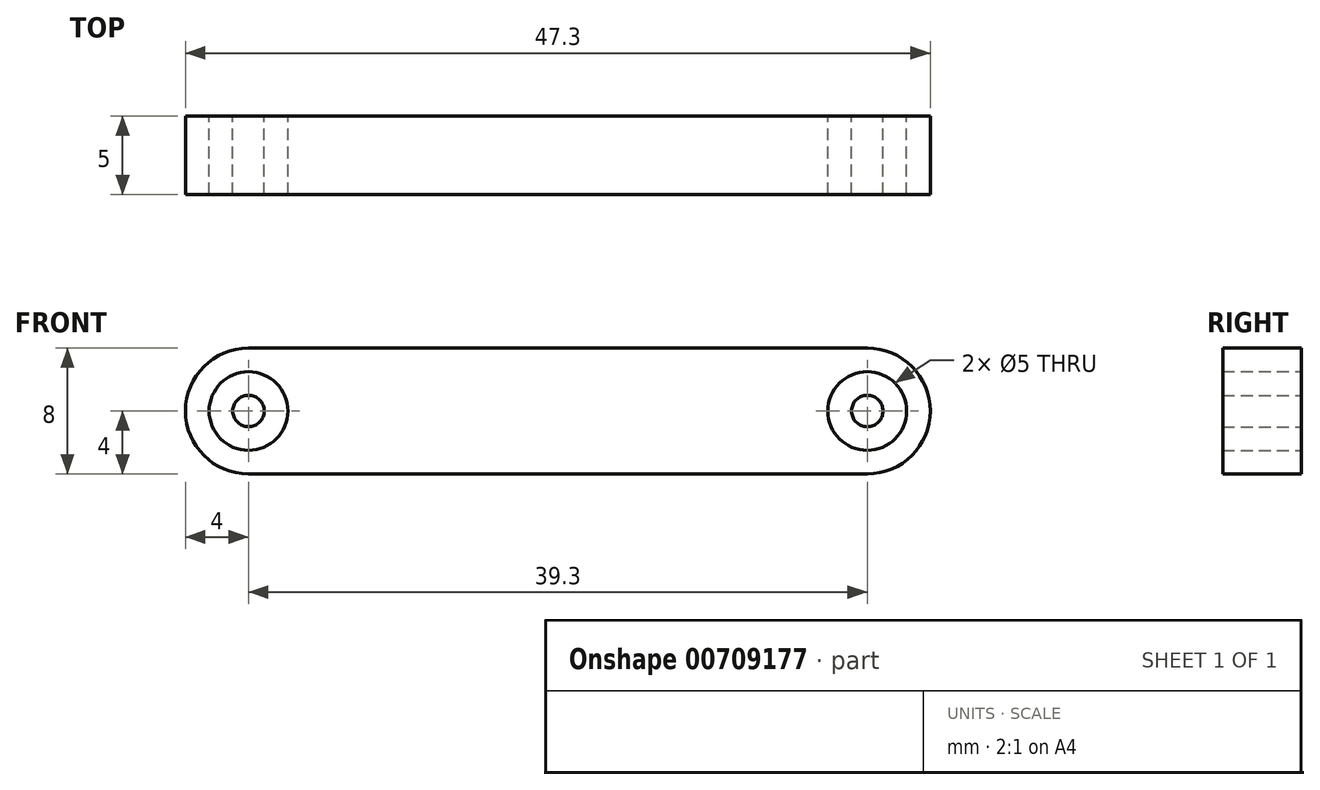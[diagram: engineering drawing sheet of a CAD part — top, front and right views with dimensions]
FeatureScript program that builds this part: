
annotation { "Feature Type Name" : "Feature", "Feature Type Description" : "" }
export const myFeature = defineFeature(function(context is Context, id is Id, definition is map)
    precondition{}
    {
        {
            var Q0;
            Q0=qCreatedBy(makeId("Front.planeOp"),FACE);
            var sketch = newSketch(context, id + "F0", { "sketchPlane" : qUnion([Q0])});
            skArc(sketch, "E0", {"start": v(0, 4) * mm, "mid": v(-4, 0) * mm, "end": v(0, -4) * mm});
            skArc(sketch, "E1", {"start": v(39.3, -4) * mm, "mid": v(43.3, 0) * mm, "end": v(39.3, 4) * mm});
            skLineSegment(sketch, "E2", {"start": v(0, 4) * mm, "end": v(39.3, 4) * mm});
            skLineSegment(sketch, "E3", {"start": v(0, -4) * mm, "end": v(39.3, -4) * mm});
            skCircle(sketch, "E4", {"center": v(0, 0) * mm, "radius": 2.5 * mm});
            skCircle(sketch, "E5", {"center": v(0, 0) * mm, "radius": 1 * mm});
            skCircle(sketch, "E6", {"center": v(39.3, 0) * mm, "radius": 2.5 * mm});
            skCircle(sketch, "E7", {"center": v(39.3, 0) * mm, "radius": 1 * mm});
            skSolve(sketch);
        }
        {
            var Q0;
            Q0=makeQuery(id+"F0.imprint","IMPRINT",FACE,{"disambiguationData":[TD([[makeQuery(id+"F0.imprint","IMPRINT",EDGE,{"derivedFrom":sQuery(id+"F0.wireOp",EDGE,"E0")}),1.0]])]});
            var Q1;
            Q1=makeQuery(id+"F0.imprint","IMPRINT",FACE,{"disambiguationData":[TD([[makeQuery(id+"F0.imprint","IMPRINT",EDGE,{"derivedFrom":sQuery(id+"F0.wireOp",EDGE,"E5")}),1.0]])]});
            var Q2;
            Q2=makeQuery(id+"F0.imprint","IMPRINT",FACE,{"disambiguationData":[TD([[makeQuery(id+"F0.imprint","IMPRINT",EDGE,{"derivedFrom":sQuery(id+"F0.wireOp",EDGE,"E7")}),1.0]])]});
            extrude(context, id + "F1", {"entities" : qUnion([Q0, Q1, Q2]), "depth" : 5 * mm, "offsetDistance" : 25 * mm});
        }
    });
